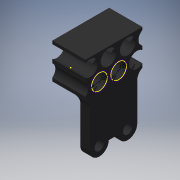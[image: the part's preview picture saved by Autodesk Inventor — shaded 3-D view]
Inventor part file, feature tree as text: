
AUTODESK INVENTOR PART (.ipt)
format: ipt  version: 2016 (Build 200138000, 138)  size: 217,088 bytes
history: native  units: in
note: dims shown in document units (in); Inventor stores cm internally (conversion verified against a paired STEP export)
features: other x3, sketch x1
ambient origin geometry x8: Origin, YZ Plane, XZ Plane, XY Plane, X Axis, Y Axis, Z Axis, Center Point
bodies: Solid1 (feature_tree)
feature tree (4):
  other  "motor holders.ipt"
  sketch  "Sketch1"  dims[d0=0.4331in d1=0.1575in d2=0.1575in]
  other  "Solid2::motor holders.ipt"
  other  "TaggingFeature1"
